# Revit family: NBS_HeatraeSadia_DrnkngFntnPckgs_Superchill_30B
name_source: partatom
category: Plumbing Fixtures
revit_build: Autodesk Revit 2014 (Build: 20130709_2115(x64)
units: mm (PartAtom-declared; Revit-internal decimal feet)

## types (1)
- Superchill30B
    AssetType = Fixed
    BIMObjectName = NBS_HeatraeSadia_DrinkingFountainPackages_Superchill30B
    CW Connection = Yes
    Color = Natural
    CompressorPower = 1/12 hp
    Connections = 8 mm female push fit inlet connection with supplied 8 mm male adapter, 6 mm female push fit outlet tube
    Controls = Push button operated filler tap
    Depth = 394 mm
    Description = Chilled drinking water fountain
    DurationUnit = year
    ElectricalDeviceNominalPower = 180
    Features = Separate cooling and dispensing units making it ideal for use in concealed applications, supplied with a filler tap, ice bank cooling system
    Finish = Brushed
    FlowRate = 30 L/hr
    FormUnit = Undercounter on a level horizontal surface
    FormWastes = Integral 1¼" BSP waste outlet connection
    FormWaterSupply = Chilled, filtered supply to jet
    HW Connection = No
    HasProtectiveEarth = No
    Height = 404 mm  [stored 1.32546 ft]
    IPCode = IPX2
    IfcExportAs = IfcElectricApplianceType
    IfcExportType = FREESTANDINGWATERCOOLER
    IntegralAccessories = Cup holder (95:970:127), Drip tray no waste (95:970:128), Drip tray with waste (95:970:123), Water filter system (95:970:129)
    ManufacturerName = Heatrae Sadia
    ManufacturerURL = www.heatraesadia.com
    Material = Outer casing: Stainless steel effect plastic-coated, corrosion proofed steel
    ModelNumber = 95:200:227
    ModelReference = Superchill 30B
    NBSCertification = http://www.nationalbimlibrary.com
    NBSDescription = Drinking fountain packages
    NBSReference = 45-35-70/400
    Name = DrinkingFountainPackages_Superchill30B_HeatraeSadia
    NominalCurrent = 0
    NominalFrequencyRange = 0
    NominalHeight = 404 mm  [stored 1.32546 ft]
    NominalLength = 394 mm
    NominalVoltage = 230.0, 240.0
    NominalWidth = 255 mm  [stored 0.836614 ft]
    NumberOfPoles = 0
    OutletTemperatureRange = 3-10°C
    PhaseAngle = 0.00°
    ProductInformation = www.heatraesadia.com/docs/Drinking_water_brochure.pdf
    Size = 405 x 255 x 400 mm
    StorageWaterHeaterMaterial = NBS_Concept
    SupplyPressureRange = 1.0-3.0 bar
    ThirdPartyCertification = WRAS listed
    Uniclass2 = 45-90-46/428
    Uniclass2015Description = Drinking fountains
    Uniclass2015Reference = Pr_40_20_87_24
    Uniclass2015Version = Products v1.1
    UsageCurrent = 0
    Vent Connection = No
    Version = 1
    WarrantyDurationLabor = 2
    WarrantyDurationParts = 2
    WarrantyDurationUnit = year
    WarrantyStartDate = 1900-12-31T23:59:59
    Waste Connection = No
    WaterChillingSystem = Hermetic ice bank direct cooling system
    Weight = 27 kg (full)
    Width = 255 mm  [stored 0.836614 ft]

note: [stored X ft] marks values corroborated as IEEE doubles in the binary element streams (Revit-internal decimal feet)

## geometry (parser evidence)
native form markers: Sweep x3
no freeform markers — native parametric forms only
